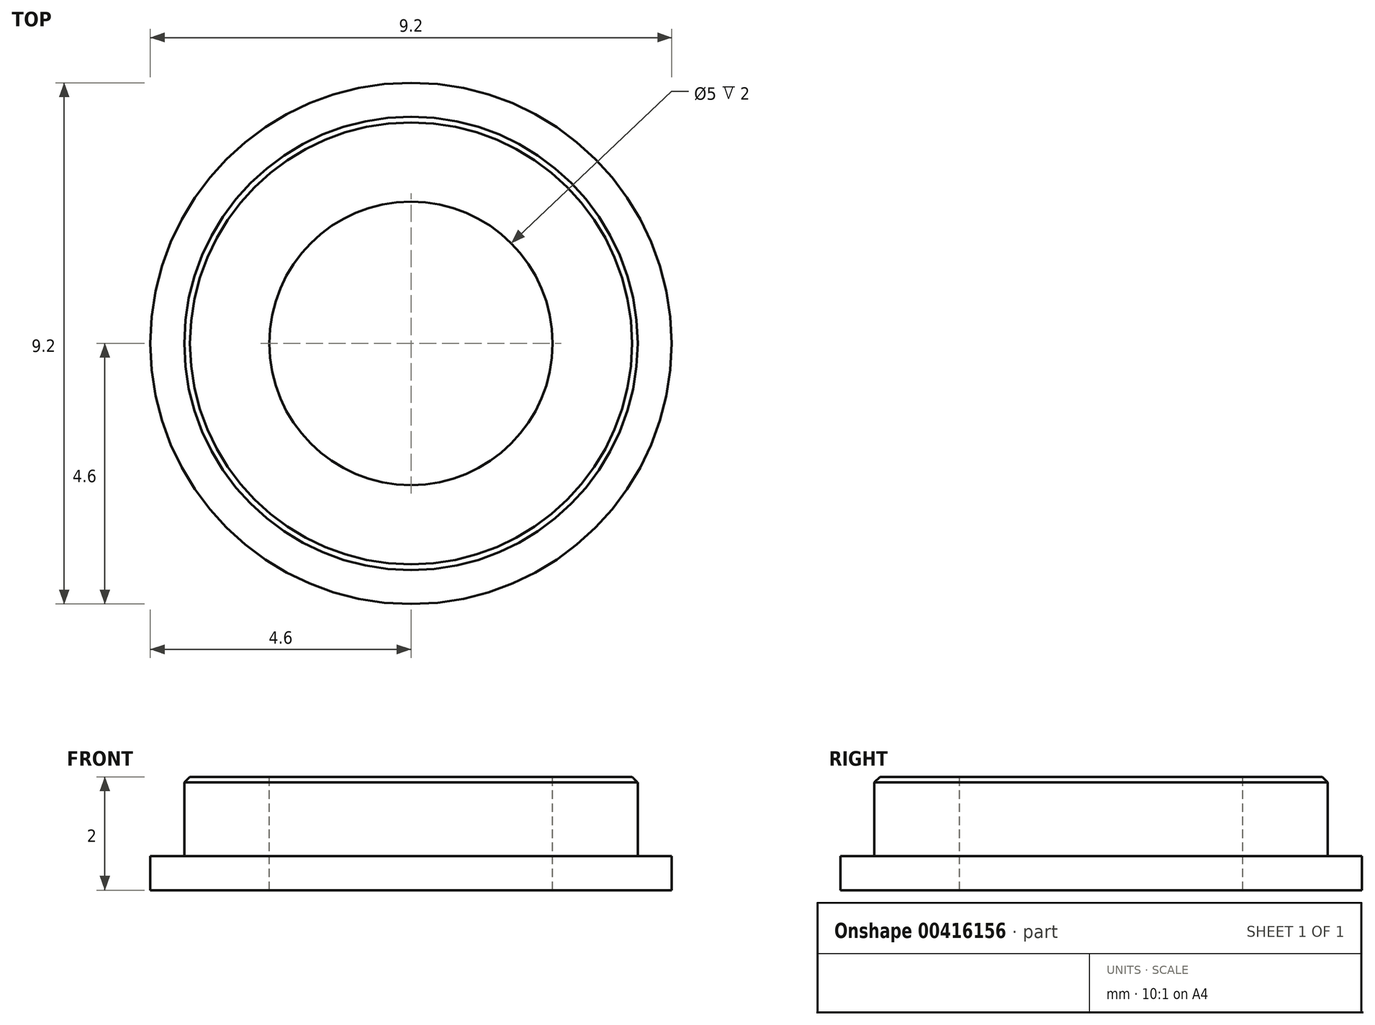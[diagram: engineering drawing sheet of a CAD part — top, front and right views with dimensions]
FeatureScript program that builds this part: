
annotation { "Feature Type Name" : "Feature", "Feature Type Description" : "" }
export const myFeature = defineFeature(function(context is Context, id is Id, definition is map)
    precondition{}
    {
        {
            var Q0;
            Q0=qCreatedBy(makeId("Top.planeOp"),FACE);
            var sketch = newSketch(context, id + "F0", { "sketchPlane" : qUnion([Q0])});
            skCircle(sketch, "E0", {"center": v(0, 0) * mm, "radius": 4.6 * mm});
            skCircle(sketch, "E1", {"center": v(0, 0) * mm, "radius": 4 * mm});
            skSolve(sketch);
        }
        {
            var Q0;
            Q0=makeQuery(id+"F0.imprint","IMPRINT",FACE,{"disambiguationData":[TD([[makeQuery(id+"F0.imprint","IMPRINT",EDGE,{"derivedFrom":sQuery(id+"F0.wireOp",EDGE,"E1")}),1.0]])]});
            extrude(context, id + "F1", {"entities" : qUnion([Q0]), "depth" : 2 * mm, "offsetDistance" : 25 * mm});
        }
        {
            var Q0;
            Q0=makeQuery(id+"F0.imprint","IMPRINT",FACE,{"disambiguationData":[TD([[makeQuery(id+"F0.imprint","IMPRINT",EDGE,{"derivedFrom":sQuery(id+"F0.wireOp",EDGE,"E0")}),1.0]])]});
            extrude(context, id + "F2", {"entities" : qUnion([Q0]), "operationType" : NewBodyOperationType.ADD, "depth" : 0.6 * mm, "offsetDistance" : 25 * mm});
        }
        {
            var Q0;
            Q0=sQuery(id+"F0.wireOp",VERTEX,"E0.center");
            var Q1;
            Q1=makeQuery(id+"F1.opExtrude","SWEPT_BODY",BODY,{"disambiguationData":[OSD([sQuery(id+"F0.wireOp",EDGE,"E1")])]});
            hole(context, id + "F3", {"style" : HoleStyle.SIMPLE, "endStyle" : HoleEndStyle.THROUGH, "oppositeDirection" : true, "holeDiameter" : 5 * mm, "majorDiameter" : 5 * mm, "isTappedThrough" : true, "tappedDepth" : 12 * mm, "tapClearance" : 3, "locations" : qUnion([Q0]), "scope" : qUnion([Q1])});
        }
        {
            var Q0;
            Q0=makeQuery(id+"F3.hole-0.boolean.opBoolean","INTERSECT",EDGE,{"derivedFrom":[makeQuery(id+"F1.opExtrude","CAP_FACE",FACE,{"disambiguationData":[OSD([sQuery(id+"F0.wireOp",EDGE,"E1")])],"isStart":false}),makeQuery(id+"F3.hole-0.opRevolve","SWEPT_FACE",FACE,{"disambiguationData":[OSD([sQuery(id+"F3.hole-0.sketch.wireOp",EDGE,"core_line_2")])]})]});
            var Q1;
            Q1=makeQuery(id+"F1.opExtrude","CAP_EDGE",EDGE,{"disambiguationData":[OSD([sQuery(id+"F0.wireOp",EDGE,"E1")])],"isStart":false});
            var Q2;
            Q2=makeQuery(id+"F3.hole-0.boolean.opBoolean","COPY",EDGE,{"derivedFrom":makeQuery(id+"F3.hole-0.opRevolve","SWEPT_EDGE",EDGE,{"disambiguationData":[OSD([sQuery(id+"F3.hole-0.sketch.wireOp",EDGE,"core_line_2"),sQuery(id+"F3.hole-0.sketch.wireOp",EDGE,"core_line_3")])]})});
            chamfer(context, id + "F4", {"entities" : qUnion([Q0, Q1, Q2]), "width" : 0.1 * mm, "tangentPropagation" : true});
        }
    });
